FCSTD DOCUMENT  (FreeCAD 0.15R4671 (Git))
Label: Bottom
License: All rights reserved
LicenseURL: http://en.wikipedia.org/wiki/All_rights_reserved
objects: Sketcher::SketchObject×1, App::VRMLObject×1
note: 1 computed .brp shape members not serialized (recipe doc carries the construction recipe); baked Part::Feature solids carry a one-line shape summary decoded from their .brp

FEATURE [Sketcher::SketchObject] Sketch
  sketch-geometry (12):
    g0: Circle CenterX=5 CenterY=125 CenterZ=0 NormalX=0 NormalY=0 NormalZ=1 Radius=2
    g1: LineSegment StartX=0 StartY=132.5 StartZ=0 EndX=90 EndY=132.5 EndZ=0
    g2: LineSegment StartX=90 StartY=132.5 StartZ=0 EndX=90 EndY=0 EndZ=0
    g3: LineSegment StartX=90 StartY=0 StartZ=0 EndX=0 EndY=0 EndZ=0
    g4: LineSegment StartX=0 StartY=0 StartZ=0 EndX=0 EndY=132.5 EndZ=0
    g5: Circle CenterX=85 CenterY=125 CenterZ=0 NormalX=0 NormalY=0 NormalZ=1 Radius=2
    g6: Circle CenterX=85 CenterY=5 CenterZ=0 NormalX=0 NormalY=0 NormalZ=1 Radius=2
    g7: Circle CenterX=5 CenterY=5 CenterZ=0 NormalX=0 NormalY=0 NormalZ=1 Radius=2
    g8: LineSegment StartX=-2 StartY=134.5 StartZ=0 EndX=92 EndY=134.5 EndZ=0
    g9: LineSegment StartX=92 StartY=134.5 StartZ=0 EndX=92 EndY=-2 EndZ=0
    g10: LineSegment StartX=92 StartY=-2 StartZ=0 EndX=-2 EndY=-2 EndZ=0
    g11: LineSegment StartX=-2 StartY=-2 StartZ=0 EndX=-2 EndY=134.5 EndZ=0
  constraints (35):
    c: Coincident(g1,g2)
    c: Coincident(g2,g3)
    c: Coincident(g3,g4)
    c: Coincident(g4,g1)
    c: Horizontal(g1)
    c: Horizontal(g3)
    c: Vertical(g2)
    c: Vertical(g4)
    c: Distance(g0,g4) = 5
    c: Radius(g0) = 2
    c: Distance(g0,g1) = 7.5
    c: Distance(g4) = 132.5
    c: Distance(g1,g1) = 90
    c: Radius(g5) = 2
    c: Distance(g5,g2) = 5
    c: Distance(g5,g1) = 7.5
    c: Radius(g6) = 2
    c: Distance(g6,g2) = 5
    c: Coincident(g3,g-1)
    c: Distance(g7,g4) = 5
    c: Distance(g7,g3) = 5
    c: Radius(g7) = 2
    c: Distance(g6,g3) = 5
    c: Coincident(g8,g9)
    c: Coincident(g9,g10)
    c: Coincident(g10,g11)
    c: Coincident(g11,g8)
    c: Horizontal(g8)
    c: Horizontal(g10)
    c: Vertical(g9)
    c: Vertical(g11)
    c: Distance(g1,g9) = 2
    c: Distance(g1,g8) = 2
    c: Distance(g8,g4) = 2
    c: Distance(g10,g3) = 2
FEATURE [App::VRMLObject] Cherry_MX_Keyboard_PCB
  Placement = pos=(-47.5,165,0) rot=(0,0,1;0rad)
